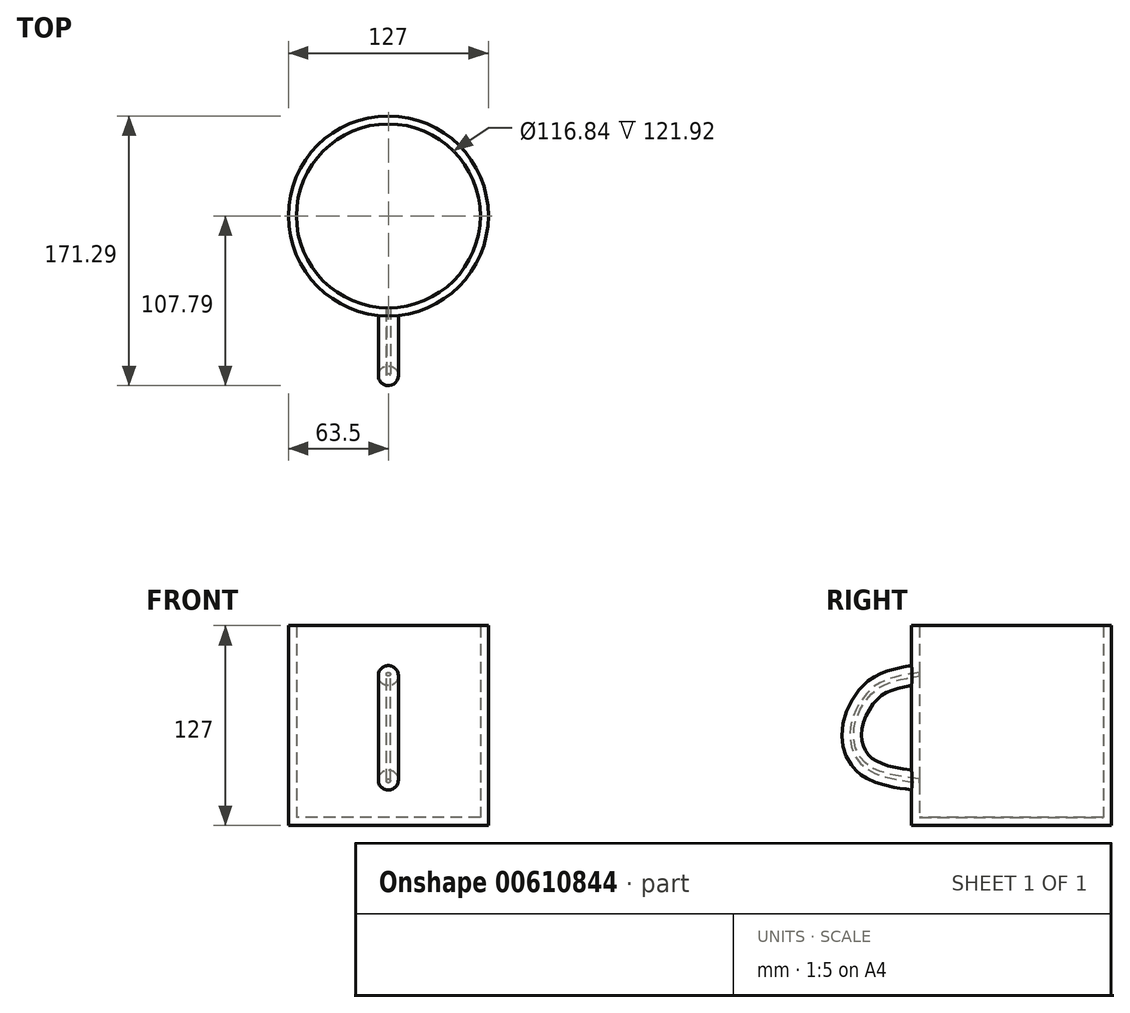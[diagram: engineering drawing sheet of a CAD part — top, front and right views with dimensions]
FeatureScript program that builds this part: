
annotation { "Feature Type Name" : "Feature", "Feature Type Description" : "" }
export const myFeature = defineFeature(function(context is Context, id is Id, definition is map)
    precondition{}
    {
        {
            var Q0;
            Q0=qCreatedBy(makeId("Top.planeOp"),FACE);
            var sketch = newSketch(context, id + "F0", { "sketchPlane" : qUnion([Q0])});
            skCircle(sketch, "E0", {"center": v(0, 0) * mm, "radius": 63.5 * mm});
            skSolve(sketch);
        }
        {
            var Q0;
            Q0 = qSketchRegion(id + "F0", true);
            extrude(context, id + "F1", {"entities" : qUnion([Q0]), "depth" : 127 * mm, "offsetDistance" : 25.4 * mm});
        }
        {
            var Q0;
            Q0=qCreatedBy(makeId("Right.planeOp"),FACE);
            var sketch = newSketch(context, id + "F2", { "sketchPlane" : qUnion([Q0])});
            skFitSpline(sketch, "E1", {"points": [v(-62.37, 95.61) * mm, v(-87.5, 86.75) * mm, v(-101.61, 58.72) * mm, v(-91.5, 37.08) * mm, v(-57.65, 28.18) * mm], "startDerivative": vector(-112.19, -18.84) * mm, "endDerivative": vector(140.02, -16.39) * mm});
            skSolve(sketch);
        }
        {
            var Q0;
            Q0=qCreatedBy(makeId("Front.planeOp"),FACE);
            cPlane(context, id + "F3", {"entities" : qUnion([Q0]), "cplaneType" : CPlaneType.OFFSET, "offset" : 63.5 * mm, "width" : 152.4 * mm, "height" : 152.4 * mm});
        }
        {
            var Q0;
            Q0=qCreatedBy(id+"F3.planeOp",FACE);
            var sketch = newSketch(context, id + "F4", { "sketchPlane" : qUnion([Q0])});
            skCircle(sketch, "E2", {"center": v(0, 95.3) * mm, "radius": 6.35 * mm});
            skSolve(sketch);
        }
        {
            var Q0;
            Q0=makeQuery(id+"F4.imprint","IMPRINT",FACE,{"disambiguationData":[TD([[makeQuery(id+"F4.imprint","IMPRINT",EDGE,{"derivedFrom":sQuery(id+"F4.wireOp",EDGE,"E2")}),1.0]])]});
            var Q1;
            Q1=sQuery(id+"F2.wireOp",EDGE,"E1");
            sweep(context, id + "F5", {"operationType" : NewBodyOperationType.ADD, "profiles" : qUnion([Q0]), "path" : qUnion([Q1])});
        }
        {
            var Q0;
            Q0=makeQuery(id+"F1.opExtrude","CAP_FACE",FACE,{"disambiguationData":[OSD([sQuery(id+"F0.wireOp",EDGE,"E0")])],"isStart":false});
            shell(context, id + "F6", {"entities" : qUnion([Q0]), "thickness" : 5.08 * mm});
        }
    });
